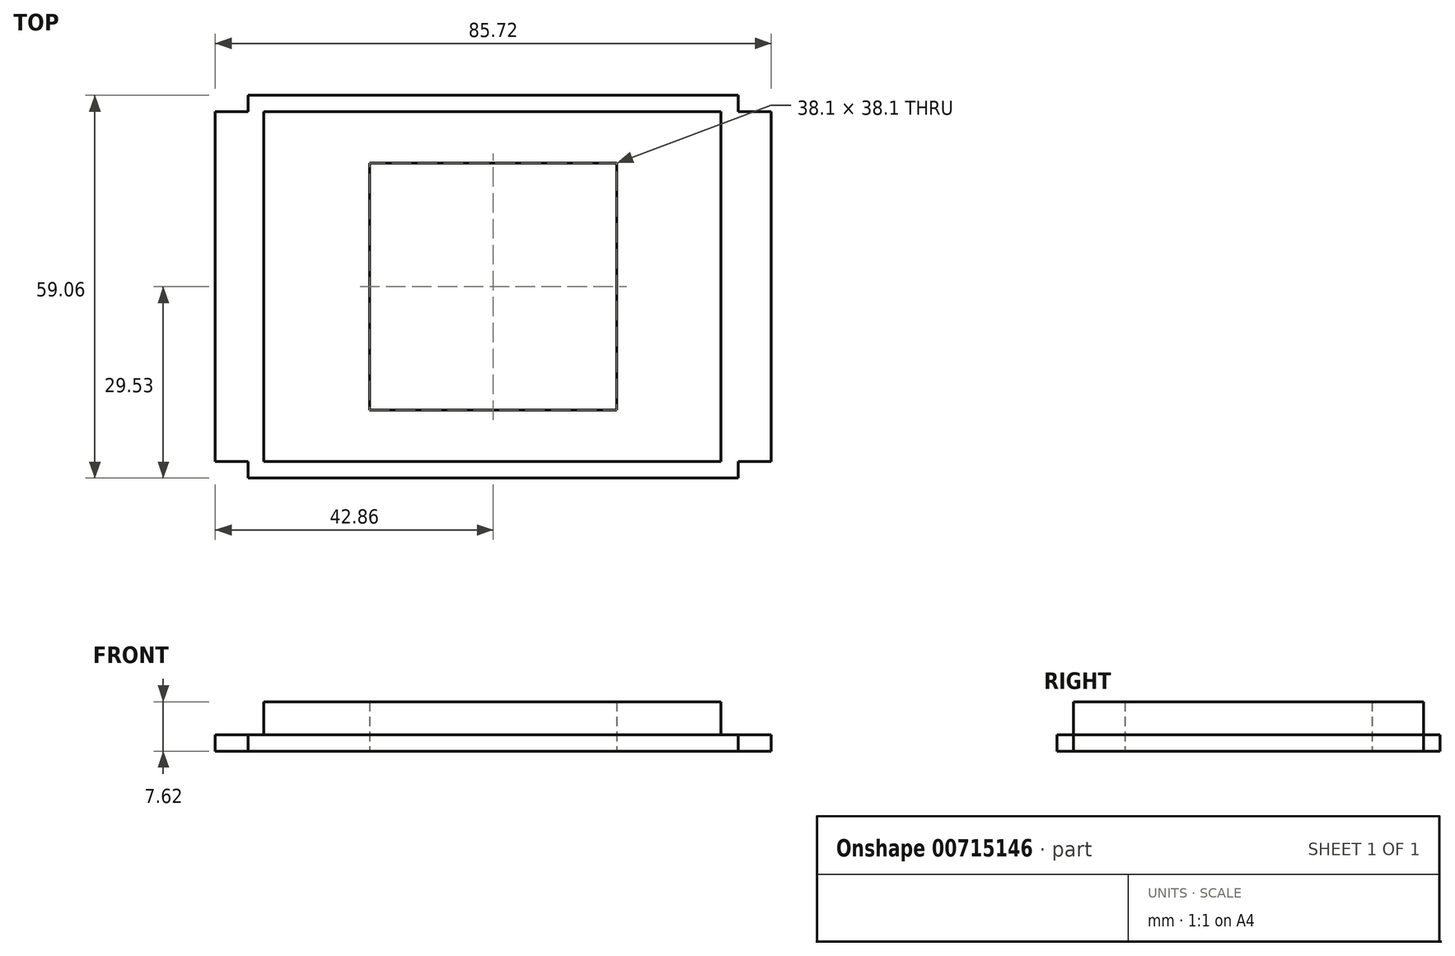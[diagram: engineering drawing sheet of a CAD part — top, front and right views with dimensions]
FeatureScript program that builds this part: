
annotation { "Feature Type Name" : "Feature", "Feature Type Description" : "" }
export const myFeature = defineFeature(function(context is Context, id is Id, definition is map)
    precondition{}
    {
        {
            var Q0;
            Q0=qCreatedBy(makeId("Top.planeOp"),FACE);
            var sketch = newSketch(context, id + "F0", { "sketchPlane" : qUnion([Q0])});
            skLineSegment(sketch, "E0.bottom", {"start": v(-37.78, -29.53) * mm, "end": v(37.78, -29.53) * mm});
            skLineSegment(sketch, "E0.top", {"start": v(-37.78, 29.53) * mm, "end": v(37.78, 29.53) * mm});
            skLineSegment(sketch, "E0.left", {"start": v(-37.78, -29.53) * mm, "end": v(-37.78, 29.53) * mm});
            skLineSegment(sketch, "E0.right", {"start": v(37.78, -29.53) * mm, "end": v(37.78, 29.53) * mm});
            skPoint(sketch, "E0.middle", {"position": v(0, 0) * mm});
            skLineSegment(sketch, "E1", {"start": v(-35.37, 0) * mm, "end": v(-35.37, -26.99) * mm});
            skLineSegment(sketch, "E2", {"start": v(-35.37, -26.99) * mm, "end": v(-0.13, -26.99) * mm});
            skLineSegment(sketch, "E3", {"start": v(-0.13, 26.99) * mm, "end": v(35.11, 26.99) * mm});
            skLineSegment(sketch, "E4", {"start": v(35.11, 26.99) * mm, "end": v(35.11, 0) * mm});
            skLineSegment(sketch, "E5", {"start": v(-35.37, 0) * mm, "end": v(-35.37, 26.99) * mm});
            skLineSegment(sketch, "E6", {"start": v(-35.37, 26.99) * mm, "end": v(-0.13, 26.99) * mm});
            skLineSegment(sketch, "E7", {"start": v(35.11, 0) * mm, "end": v(35.11, -26.99) * mm});
            skLineSegment(sketch, "E8", {"start": v(35.11, -26.99) * mm, "end": v(-0.13, -26.99) * mm});
            skLineSegment(sketch, "E9.bottom", {"start": v(19.05, -19.05) * mm, "end": v(-19.05, -19.05) * mm});
            skLineSegment(sketch, "E9.top", {"start": v(19.05, 19.05) * mm, "end": v(-19.05, 19.05) * mm});
            skLineSegment(sketch, "E9.left", {"start": v(19.05, -19.05) * mm, "end": v(19.05, 19.05) * mm});
            skLineSegment(sketch, "E9.right", {"start": v(-19.05, -19.05) * mm, "end": v(-19.05, 19.05) * mm});
            skLineSegment(sketch, "E10", {"start": v(37.78, -26.99) * mm, "end": v(42.86, -26.99) * mm});
            skLineSegment(sketch, "E11", {"start": v(42.86, -26.99) * mm, "end": v(42.86, 26.99) * mm});
            skLineSegment(sketch, "E12", {"start": v(42.86, 26.99) * mm, "end": v(37.78, 26.99) * mm});
            skLineSegment(sketch, "E13", {"start": v(-37.78, 26.99) * mm, "end": v(-42.86, 26.99) * mm});
            skLineSegment(sketch, "E14", {"start": v(-42.86, 26.99) * mm, "end": v(-42.86, -26.99) * mm});
            skLineSegment(sketch, "E15", {"start": v(-42.86, -26.99) * mm, "end": v(-37.78, -26.99) * mm});
            skSolve(sketch);
        }
        {
            var Q0;
            Q0=makeQuery(id+"F0.imprint","IMPRINT",FACE,{"disambiguationData":[TD([[makeQuery(id+"F0.imprint","IMPRINT",EDGE,{"derivedFrom":sQuery(id+"F0.wireOp",EDGE,"E1")}),1.0]])]});
            extrude(context, id + "F1", {"entities" : qUnion([Q0]), "depth" : 5.08 * mm, "offsetDistance" : 25.4 * mm});
        }
        {
            var Q0;
            Q0=makeQuery(id+"F0.imprint","IMPRINT",FACE,{"disambiguationData":[TD([[makeQuery(id+"F0.imprint","IMPRINT",EDGE,{"derivedFrom":sQuery(id+"F0.wireOp",EDGE,"E1")}),1.0]])]});
            extrude(context, id + "F2", {"entities" : qUnion([Q0]), "operationType" : NewBodyOperationType.ADD, "depth" : -2.54 * mm, "offsetDistance" : 25.4 * mm});
        }
        {
            var Q0;
            Q0=makeQuery(id+"F0.imprint","IMPRINT",FACE,{"disambiguationData":[TD([[makeQuery(id+"F0.imprint","IMPRINT",EDGE,{"derivedFrom":sQuery(id+"F0.wireOp",EDGE,"E0.bottom")}),1.0]])]});
            extrude(context, id + "F3", {"entities" : qUnion([Q0]), "operationType" : NewBodyOperationType.ADD, "depth" : -2.54 * mm, "offsetDistance" : 25.4 * mm});
        }
        {
            var Q0;
            {var subQ0=sQuery(id+"F0.wireOp",EDGE,"E13");Q0=makeQuery(id+"F0.imprint","IMPRINT",FACE,{"disambiguationData":[TD([[makeQuery(id+"F0.imprint","IMPRINT",EDGE,{"derivedFrom":subQ0}),1.0]])]});}
            var Q1;
            {var subQ0=sQuery(id+"F0.wireOp",EDGE,"E10");Q1=makeQuery(id+"F0.imprint","IMPRINT",FACE,{"disambiguationData":[TD([[makeQuery(id+"F0.imprint","IMPRINT",EDGE,{"derivedFrom":subQ0}),1.0]])]});}
            extrude(context, id + "F4", {"entities" : qUnion([Q0, Q1]), "operationType" : NewBodyOperationType.ADD, "depth" : -2.54 * mm, "offsetDistance" : 25.4 * mm});
        }
    });
